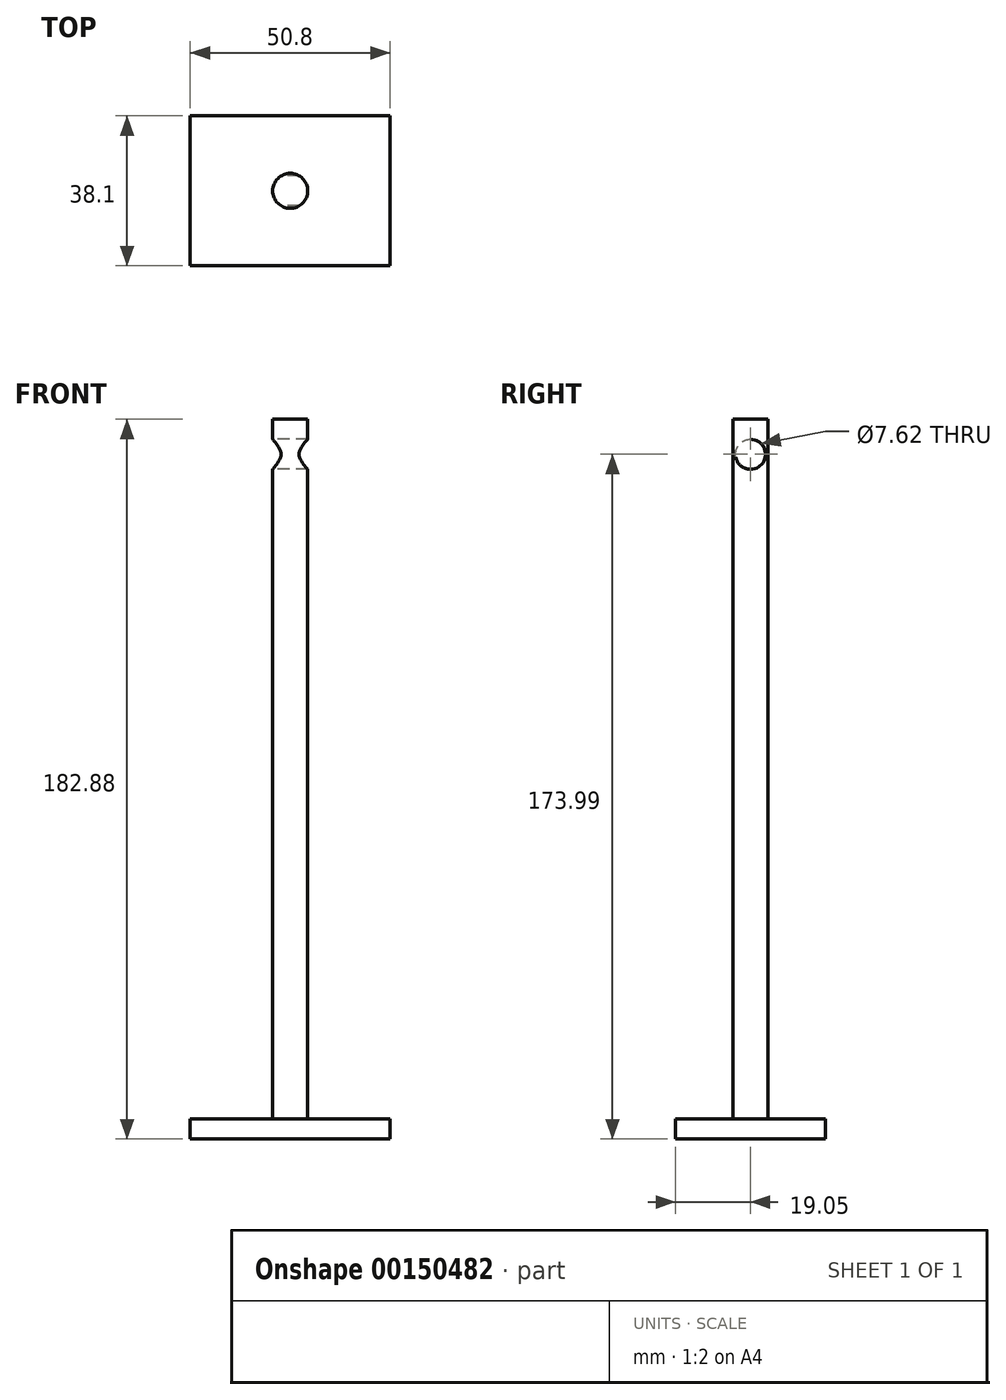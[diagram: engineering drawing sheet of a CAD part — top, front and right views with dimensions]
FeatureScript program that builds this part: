
annotation { "Feature Type Name" : "Feature", "Feature Type Description" : "" }
export const myFeature = defineFeature(function(context is Context, id is Id, definition is map)
    precondition{}
    {
        {
            var Q0;
            Q0=qCreatedBy(makeId("Front.planeOp"),FACE);
            var sketch = newSketch(context, id + "F0", { "sketchPlane" : qUnion([Q0])});
            skLineSegment(sketch, "E0", {"start": v(0, 0) * mm, "end": v(50.8, 0) * mm});
            skLineSegment(sketch, "E1", {"start": v(50.8, 0) * mm, "end": v(50.8, 5.08) * mm});
            skLineSegment(sketch, "E2", {"start": v(50.8, 5.08) * mm, "end": v(0, 5.08) * mm});
            skLineSegment(sketch, "E3", {"start": v(0, 5.08) * mm, "end": v(0, 0) * mm});
            skSolve(sketch);
        }
        {
            var Q0;
            Q0=makeQuery(id+"F0.imprint","IMPRINT",FACE,{"disambiguationData":[TD([[makeQuery(id+"F0.imprint","IMPRINT",EDGE,{"derivedFrom":sQuery(id+"F0.wireOp",EDGE,"E0")}),1.0]])]});
            extrude(context, id + "F1", {"entities" : qUnion([Q0]), "depth" : 38.1 * mm});
        }
        {
            var Q0;
            Q0=makeQuery(id+"F1.opExtrude","SWEPT_FACE",FACE,{"disambiguationData":[OSD([sQuery(id+"F0.wireOp",EDGE,"E2")])]});
            var sketch = newSketch(context, id + "F2", { "sketchPlane" : qUnion([Q0])});
            skCircle(sketch, "E4", {"center": v(25.4, -19.05) * mm, "radius": 4.45 * mm});
            skPoint(sketch, "E4.centerSnap0", {"position": v(0, -19.05) * mm});
            skPoint(sketch, "E4.centerSnap1", {"position": v(25.4, 0) * mm});
            skSolve(sketch);
        }
        {
            var Q0;
            Q0=makeQuery(id+"F2.imprint","IMPRINT",FACE,{"disambiguationData":[TD([[makeQuery(id+"F2.imprint","IMPRINT",EDGE,{"derivedFrom":sQuery(id+"F2.wireOp",EDGE,"E4")}),1.0]])]});
            var Q1;
            Q1=sQuery(id+"F2.wireOp",EDGE,"E4");
            extrude(context, id + "F3", {"entities" : qUnion([Q0]), "operationType" : NewBodyOperationType.ADD, "surfaceEntities" : qUnion([Q1]), "depth" : 177.8 * mm});
        }
        {
            var Q0;
            Q0=qCreatedBy(makeId("Right.planeOp"),FACE);
            var sketch = newSketch(context, id + "F4", { "sketchPlane" : qUnion([Q0])});
            skCircle(sketch, "E5", {"center": v(-19.05, 174) * mm, "radius": 3.81 * mm});
            skSolve(sketch);
        }
        {
            var Q0;
            Q0=makeQuery(id+"F4.imprint","IMPRINT",FACE,{"disambiguationData":[TD([[makeQuery(id+"F4.imprint","IMPRINT",EDGE,{"derivedFrom":sQuery(id+"F4.wireOp",EDGE,"E5")}),1.0]])]});
            var Q1;
            Q1=sQuery(id+"F4.wireOp",EDGE,"E5");
            extrude(context, id + "F5", {"entities" : qUnion([Q0]), "operationType" : NewBodyOperationType.REMOVE, "surfaceEntities" : qUnion([Q1]), "depth" : 50.67 * mm});
        }
    });
